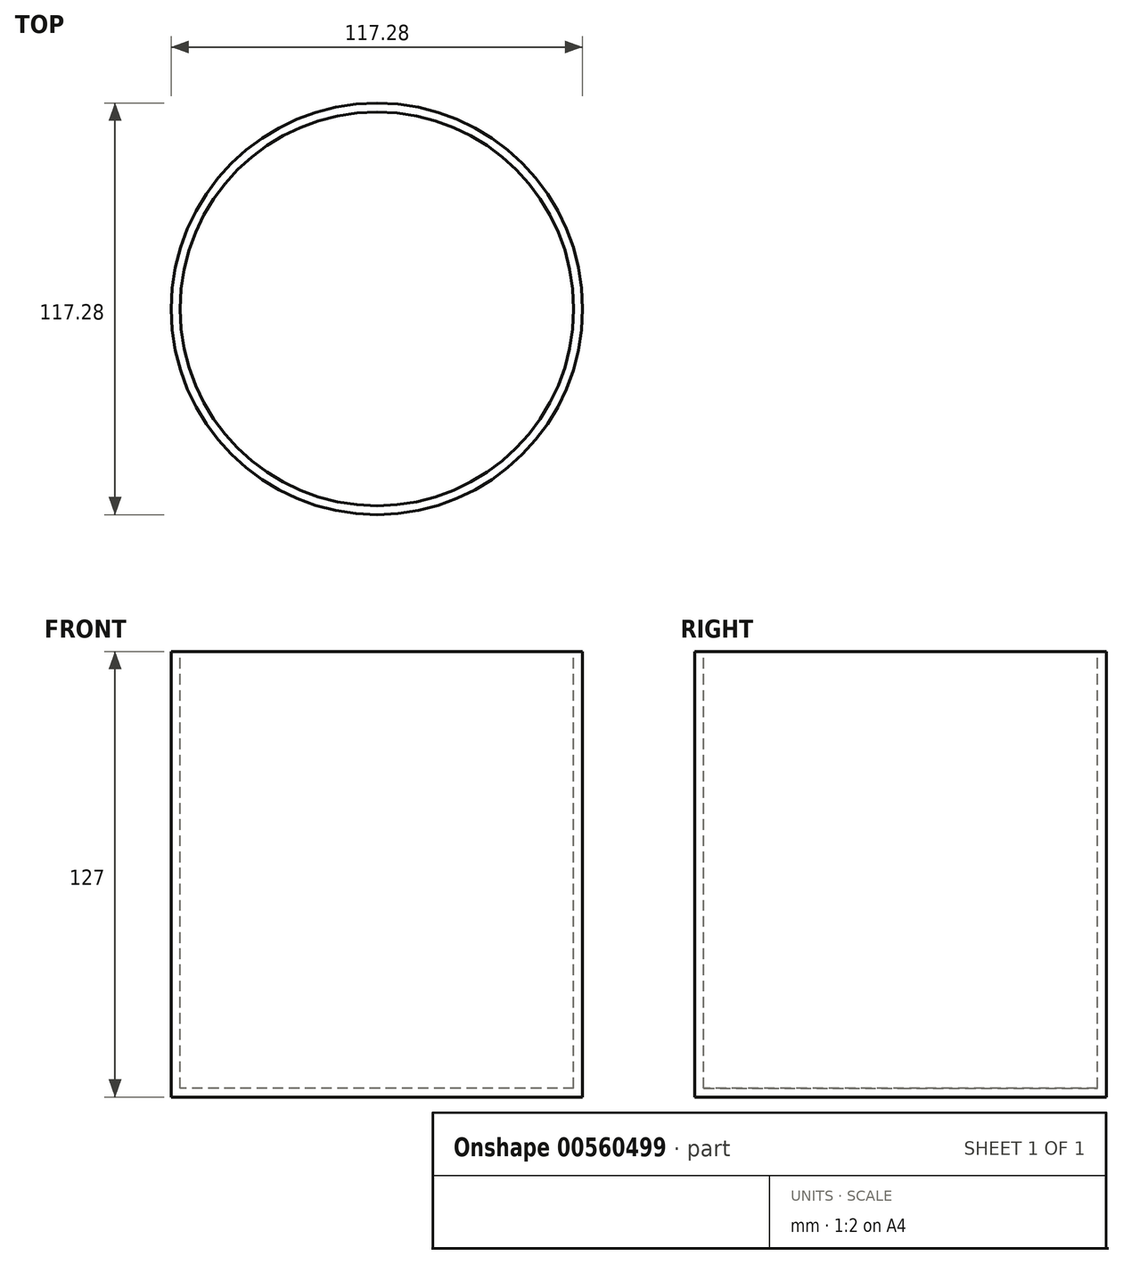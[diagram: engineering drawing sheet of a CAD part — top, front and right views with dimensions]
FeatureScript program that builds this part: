
annotation { "Feature Type Name" : "Feature", "Feature Type Description" : "" }
export const myFeature = defineFeature(function(context is Context, id is Id, definition is map)
    precondition{}
    {
        {
            var Q0;
            Q0=qCreatedBy(makeId("Top.planeOp"),FACE);
            var sketch = newSketch(context, id + "F0", { "sketchPlane" : qUnion([Q0])});
            skCircle(sketch, "E0", {"center": v(0, 0) * mm, "radius": 58.64 * mm});
            skSolve(sketch);
        }
        {
            var Q0;
            Q0 = qSketchRegion(id + "F0", true);
            extrude(context, id + "F1", {"entities" : qUnion([Q0]), "oppositeDirection" : true, "depth" : 127 * mm, "offsetDistance" : 25.4 * mm});
        }
        {
            var Q0;
            Q0=makeQuery(id+"F1.opExtrude","CAP_FACE",FACE,{"disambiguationData":[OSD([sQuery(id+"F0.wireOp",EDGE,"E0")])],"isStart":true});
            shell(context, id + "F2", {"entities" : qUnion([Q0]), "thickness" : 2.54 * mm});
        }
    });
